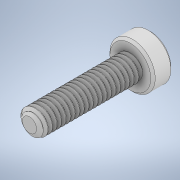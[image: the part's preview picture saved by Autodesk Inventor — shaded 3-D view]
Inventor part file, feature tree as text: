
AUTODESK INVENTOR PART (.ipt)
format: ipt  version: 2022 (Build 260153000, 153)  size: 455,680 bytes
history: mixed  units: mm
features: chamfer x1, imported_body x1
ambient origin geometry x8: Origin, YZ Plane, XZ Plane, XY Plane, X Axis, Y Axis, Z Axis, Center Point
bodies: Solid1 (imported_parasolid)
feature tree (2):
  chamfer  "Chamfer1"  [1 undecoded]
  imported_body  NMx_Import_Brep_tag  [imported B-rep: ~3 faces, bbox_mm=None]
note: 1 required parameter value undecoded (feature->parameter linkage not recoverable at this tier; creation-order binding heuristic only, values carry confidence <= 0.55)
